# Revit family: Outdoor Armor Water Heater OAN151-OAN286
name_source: partatom
category: Mechanical Equipment
revit_build: Autodesk Revit 2014 (Build: 20130308_1515(x64)
units: mm (PartAtom-declared; Revit-internal decimal feet)

## types (3) — shared parameters
# of Electrical Connections = 1
Air Inlet Radius = 1 1/2"
Description = Outdoor Armor Water Heater
FUEL TYPE = NATURAL GAS
Fuel Type = Natural or LP
Manufacturer = Lochinvar
SES BIM Studio # = 16 0649 04-1
URL = http://www.lochinvar.com
Voltage/Control = 24
Voltage/Heater = 120

## per-type parameters (varying)
| type | A_HEIGHT | C_ DEPTH | Center of Flue | D_ Drain Offset | E_Condensate Drain Offset | F_ Water Outlet Offset | Flue Radius | GAS CONN SIZE | G_Water Inlet Offset | Gas Conn Radius | H_Gas Conn Offset | INPUT RATE (BTUH) | I_Gas Conn Height | J_ Flue Depth | K_Flue Height | MODEL NO. | Model | Total Amps | VENT SIZE | WATER CONN SIZE | WIDTH | Water Conn Radius |
| OAN151 | 31 1/4" | 16 3/4" | 7 1/2" | 12" | 11 1/2" | 10" | 1 1/2" | 1/2" | 1 3/4" | 1/4" | 12" | 150,000 | 23" | 9" | 49 1/2" | OAN151 | OAN151 | 0.5 | 3" | 1 1/4" | 15 3/4" | 5/8" |
| OAN200 | 31 1/4" | 20 1/4" | 7 3/4" | 16 1/2" | 15 3/4" | 14 1/2" | 1 1/2" | 1/2" | 5 1/4" | 1/4" | 16 1/2" | 199,000 | 23" | 9 1/4" | 49 3/4" | OAN211 | OAN211 | 0.5 | 3" | 1 1/4" | 15 1/2" | 5/8" |
| OAN286 | 42 1/2" | 17 3/4" | 7 1/4" | 13 1/4" | 13 1/2" | 6 1/4" | 2" | 3/4" | 2 1/2" | 3/8" | 14" | 285,000 | 35 3/4" | 9 1/4" | 52" | OAN286 | OAN286 | 1.0 | 4" | 2" | 15 1/2" | 1" |

## geometry (parser evidence)
native form markers: Sweep x1
no freeform markers — native parametric forms only
